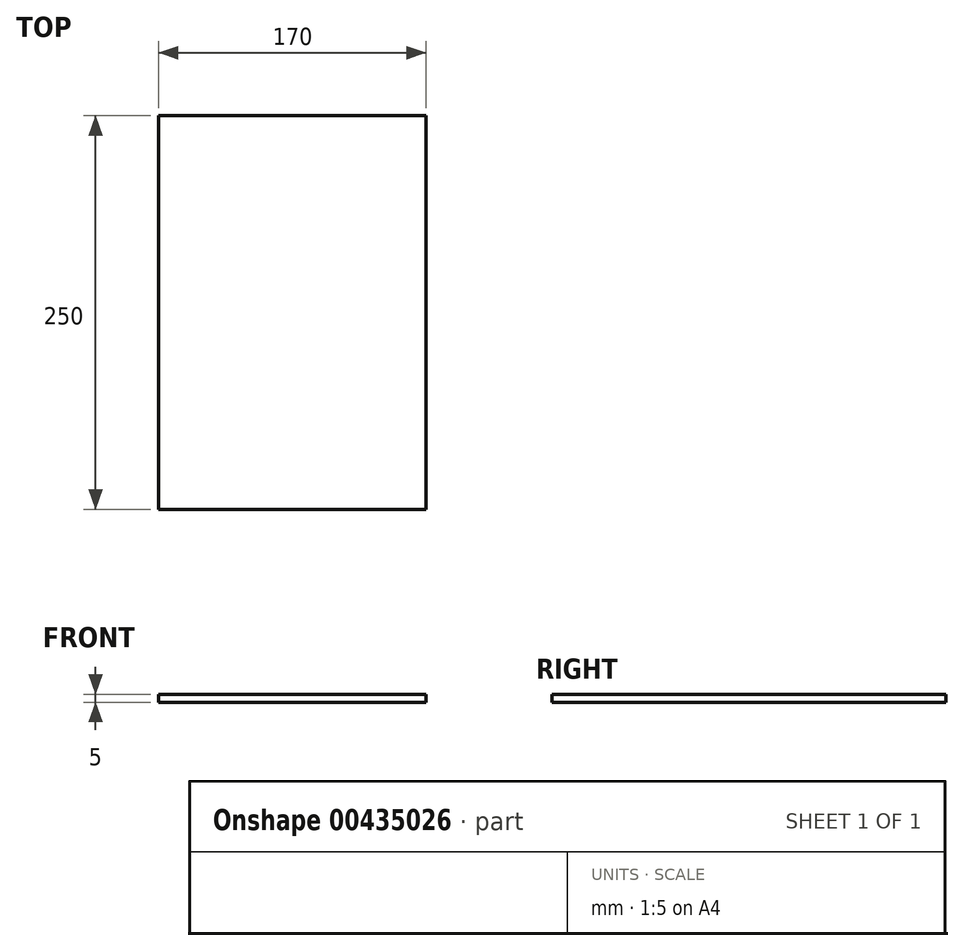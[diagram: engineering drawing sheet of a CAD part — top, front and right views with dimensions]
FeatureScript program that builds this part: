
annotation { "Feature Type Name" : "Feature", "Feature Type Description" : "" }
export const myFeature = defineFeature(function(context is Context, id is Id, definition is map)
    precondition{}
    {
        {
            var Q0;
            Q0=qCreatedBy(makeId("Top.planeOp"),FACE);
            var sketch = newSketch(context, id + "F0", { "sketchPlane" : qUnion([Q0])});
            skLineSegment(sketch, "E0.bottom", {"start": v(85, -125) * mm, "end": v(-85, -125) * mm});
            skLineSegment(sketch, "E0.top", {"start": v(85, 125) * mm, "end": v(-85, 125) * mm});
            skLineSegment(sketch, "E0.left", {"start": v(85, -125) * mm, "end": v(85, 125) * mm});
            skLineSegment(sketch, "E0.right", {"start": v(-85, -125) * mm, "end": v(-85, 125) * mm});
            skPoint(sketch, "E0.middle", {"position": v(0, 0) * mm});
            skSolve(sketch);
        }
        {
            var Q0;
            Q0=makeQuery(id+"F0.imprint","IMPRINT",FACE,{"disambiguationData":[TD([[makeQuery(id+"F0.imprint","IMPRINT",EDGE,{"derivedFrom":sQuery(id+"F0.wireOp",EDGE,"E0.bottom")}),-1.0]])]});
            extrude(context, id + "F1", {"entities" : qUnion([Q0]), "depth" : 5 * mm});
        }
    });
